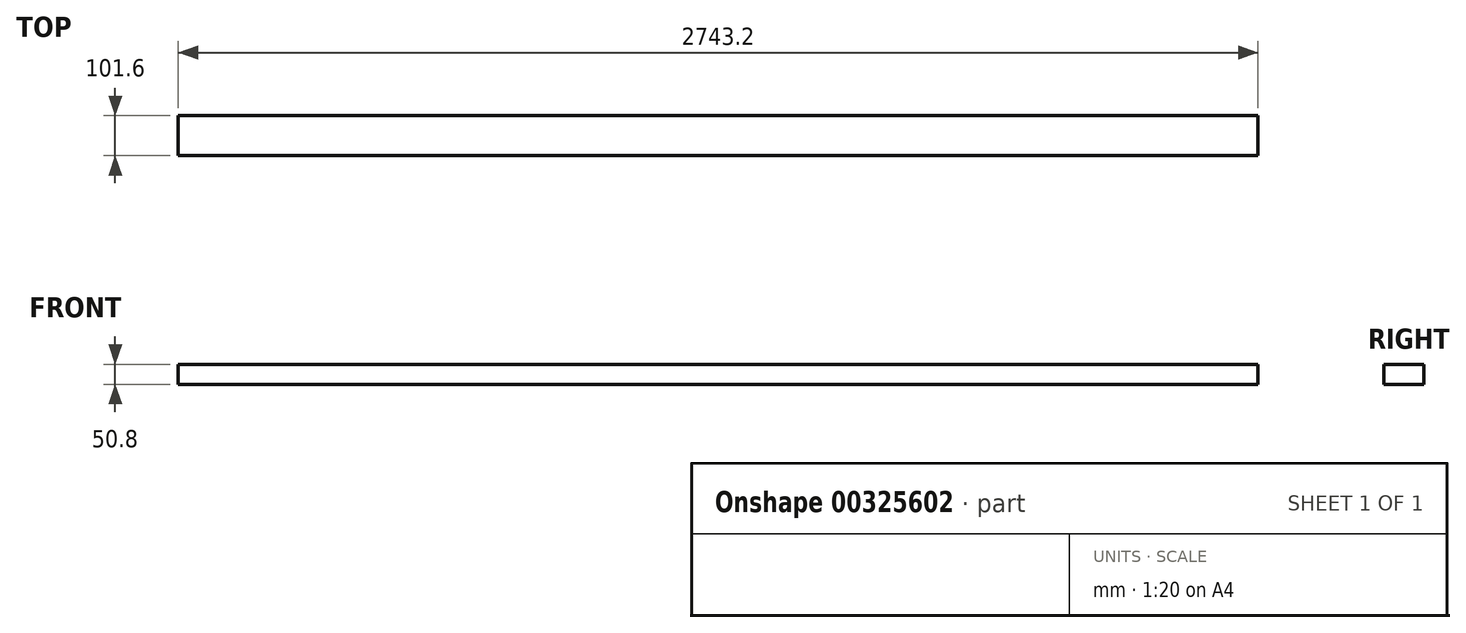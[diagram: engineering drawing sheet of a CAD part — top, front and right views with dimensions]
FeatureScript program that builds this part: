
annotation { "Feature Type Name" : "Feature", "Feature Type Description" : "" }
export const myFeature = defineFeature(function(context is Context, id is Id, definition is map)
    precondition{}
    {
        {
            var Q0;
            Q0=qCreatedBy(makeId("Top.planeOp"),FACE);
            var sketch = newSketch(context, id + "F0", { "sketchPlane" : qUnion([Q0])});
            skLineSegment(sketch, "E0.bottom", {"start": v(-965.26, 17.3) * mm, "end": v(1777.94, 17.3) * mm});
            skLineSegment(sketch, "E0.top", {"start": v(-965.26, 118.9) * mm, "end": v(1777.94, 118.9) * mm});
            skLineSegment(sketch, "E0.left", {"start": v(-965.26, 17.3) * mm, "end": v(-965.26, 118.9) * mm});
            skLineSegment(sketch, "E0.right", {"start": v(1777.94, 17.3) * mm, "end": v(1777.94, 118.9) * mm});
            skSolve(sketch);
        }
        {
            var Q0;
            Q0 = qSketchRegion(id + "F0", true);
            var Q1;
            Q1=makeQuery(id+"F0.imprint","IMPRINT",FACE,{"disambiguationData":[TD([[makeQuery(id+"F0.imprint","IMPRINT",EDGE,{"derivedFrom":sQuery(id+"F0.wireOp",EDGE,"E0.bottom")}),1.0]])]});
            extrude(context, id + "F1", {"entities" : qUnion([Q0, Q1]), "depth" : 50.8 * mm});
        }
    });
